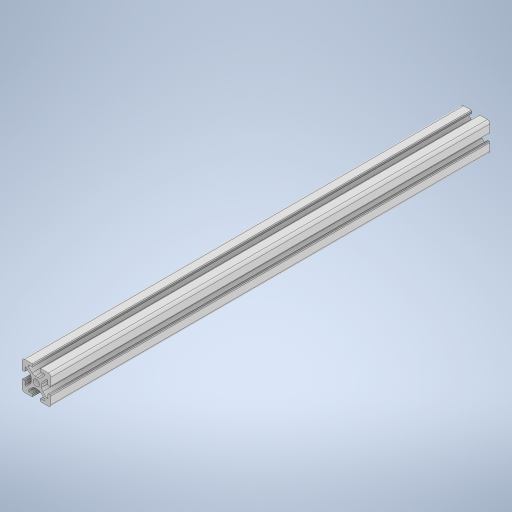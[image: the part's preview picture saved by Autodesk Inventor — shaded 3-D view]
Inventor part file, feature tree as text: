
AUTODESK INVENTOR PART (.ipt)
format: ipt  version: 2023 (Build 270158000, 158)  size: 327,680 bytes
history: mixed  units: in
note: dims shown in document units (in); Inventor stores cm internally (conversion verified against a paired STEP export)
features: mirror x1, imported_body x1
ambient origin geometry x8: Origin, YZ Plane, XZ Plane, XY Plane, X Axis, Y Axis, Z Axis, Center Point
bodies: Solid1 (imported_parasolid)
feature tree (2):
  mirror  "Mirror2"
  imported_body  NMx_Import_Brep_tag  [imported B-rep: ~75 faces, bbox_mm=[20.0, 20.0, 304.8]]
